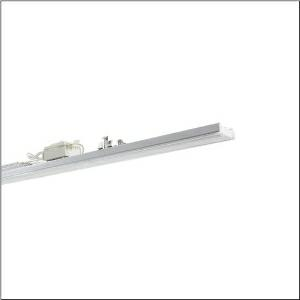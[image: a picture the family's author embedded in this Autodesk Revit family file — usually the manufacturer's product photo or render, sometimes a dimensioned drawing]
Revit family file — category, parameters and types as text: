
# Revit family: licross_21_recessed_mo_52te1edv4dxg
name_source: partatom
category: Lighting Fixtures
units: mm (PartAtom-declared; Revit-internal decimal feet)

## family parameters
Cut with Voids When Loaded = No
Host = Face
Light Source = No
Part Type = Normal
Room Calculation Point = No
Round Connector Dimension = Use Diameter
Shared = No

## types (1)
- --- (1 x LED, 13000 lm, 73.6 W, 4000K)
    Apparent Load = 74 VA
    CIE Flux Codes = 85 95 99 100 100
    Color Rendering = 80
    Color Temperature = 4000K
    Default Elevation = 1800 mm
    Description = Licross 21 Recessed MO, luminaire insert, of sheet steel, galvanised, coil coated, white, length: 2.250mm, width: 66mm, height: 67mm, LED rated luminous flux: 13.000lm, light colour: 840, SDCM (Standard Deviation of Colour Matching)MacAdam ≤ 3 SDCM (initial), control gear: DALI 2, with plug, 5-pole, with phase selection, mains connection: 220..240V, AC, 50/60Hz, rated input power: 74W, internal wiring halogen-free, primary light control with lens, of plastic, primary optical cover: cover, of PMMA, light emission: direct distribution, primary light characteristic: symmetric, protection rating (complete): IP54, insulation class (complete): insulation class I (protective earthing), certification: CE, ENEC, VDE, UKCA, protection symbol: D if used in an environment with non-conductive dust loads with corresponding accessories, impact resistance: IK06, permissible ambient temperature for indoor applications: -25..+35°C, corresponds to IFS (International Featured Standards) requirements for safety and quality in the food industry, reducing of maximum allowable ambient temperature of 5°C with ceiling mounting, LABS conformity tested according to VDMA 24364:2018-05, The light source and the operating device comply with the requirements of the Ecodesign Regulation (EU) 2019/2020 and are replaceable in accordance with this regulation, packaging unit: 1 piece
    Height = 58 mm
    Lamp = 1 x LED
    Lamp Light Flux = 13000 lm
    Lamp Power = 73.6 W
    Lamp count = 1
    Length = 2250 mm
    Luminous efficacy = 177 lm/W
    Manufacturer = Siteco
    ModVariant = No
    Model = 52TE1EDV4DXG
    Mounting Place = Ceiling
    Mounting Type = Pendant
    Number of Poles = 1
    OnlyDefault = Yes
    Power Factor = 1
    Product Name = Licross 21 Recessed MO
    Product group = luminaire insert | ceiling pendant
    ProductGroupID = 901
    Protection Class = Protection class I
    Protection Degree = IP 54
    RLX_Detail_Level = 1
    RLX_Emergency_Light_Flux = 0 lm
    RLX_Emergency_Type = 0
    RLX_Emergency_Type_DB = No
    RlxData = <blob elided: 29957 chars, md5=9f52150d>
    Socket = socket
    Standby Power = 0 W
    System Light Flux = 13000 lm
    System Power = 74 W
    Type Comments = factory setting: luminous flux: 100 % | dim-lin: 254 | 336 mA
    Type Image = l_1296930.jpg
    URL = http://relux.com
    VarID = @adj_125631
    Voltage = 0 V
    Weight = 0.00 kg
    Width = 66 mm

## geometry (parser evidence)
native form markers: Blend x4, Sweep x8
no freeform markers — native parametric forms only
